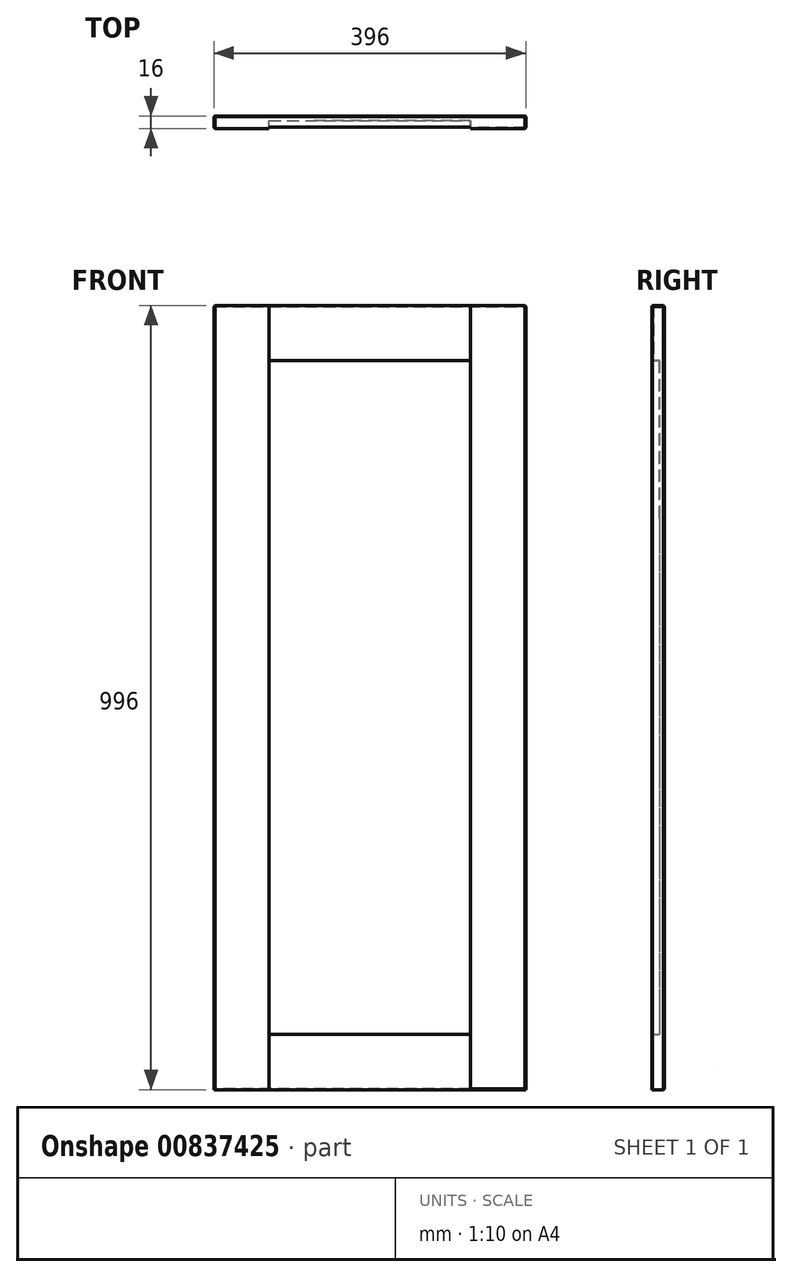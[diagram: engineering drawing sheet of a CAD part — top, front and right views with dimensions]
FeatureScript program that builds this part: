
annotation { "Feature Type Name" : "Feature", "Feature Type Description" : "" }
export const myFeature = defineFeature(function(context is Context, id is Id, definition is map)
    precondition{}
    {
        {
            var Q0;
            Q0=qCreatedBy(makeId("Front.planeOp"),FACE);
            var sketch = newSketch(context, id + "F0", { "sketchPlane" : qUnion([Q0])});
            skLineSegment(sketch, "E0.bottom", {"start": v(0, 0) * mm, "end": v(35.9, 0) * mm});
            skLineSegment(sketch, "E0.top", {"start": v(0, 30.12) * mm, "end": v(35.9, 30.12) * mm});
            skLineSegment(sketch, "E0.left", {"start": v(0, 0) * mm, "end": v(0, 30.12) * mm});
            skLineSegment(sketch, "E0.right", {"start": v(35.9, 0) * mm, "end": v(35.9, 30.12) * mm});
            skSolve(sketch);
        }
        {
            var Q0;
            Q0=makeQuery(id+"F0.imprint","IMPRINT",FACE,{"disambiguationData":[TD([[makeQuery(id+"F0.imprint","IMPRINT",EDGE,{"derivedFrom":sQuery(id+"F0.wireOp",EDGE,"E0.bottom")}),1.0]])]});
            extrude(context, id + "F1", {"entities" : qUnion([Q0]), "depth" : 16 * mm, "offsetDistance" : 25.4 * mm});
        }
        {
            var Q0;
            Q0=makeQuery(id+"F1.opExtrude","SWEPT_FACE",FACE,{"disambiguationData":[OSD([sQuery(id+"F0.wireOp",EDGE,"E0.left")])]});
            extrude(context, id + "F2", {"entities" : qUnion([Q0]), "operationType" : NewBodyOperationType.ADD, "oppositeDirection" : true, "depth" : 196 * mm, "offsetDistance" : 25 * mm});
        }
        {
            var Q0;
            {var subQ0=sQuery(id+"F0.wireOp",EDGE,"E0.bottom");Q0=makeQuery(id+"F2.boolean.opBoolean","MERGE",FACE,{"derivedFrom":[makeQuery(id+"F1.opExtrude","SWEPT_FACE",FACE,{"disambiguationData":[OSD([subQ0])]}),makeQuery(id+"F2.opExtrude","SWEPT_FACE",FACE,{"disambiguationData":[OSD([subQ0,sQuery(id+"F0.wireOp",EDGE,"E0.left")])]})]});}
            extrude(context, id + "F3", {"entities" : qUnion([Q0]), "operationType" : NewBodyOperationType.ADD, "oppositeDirection" : true, "depth" : 796 * mm, "offsetDistance" : 25 * mm});
        }
        {
            var Q0;
            {var subQ0=sQuery(id+"F0.wireOp",EDGE,"E0.left");var subQ1=sQuery(id+"F0.wireOp",EDGE,"E0.bottom");Q0=makeQuery(id+"F3.boolean.opBoolean","MERGE",FACE,{"derivedFrom":[makeQuery(id+"F2.boolean.opBoolean","MERGE",FACE,{"derivedFrom":[makeQuery(id+"F1.opExtrude","CAP_FACE",FACE,{"disambiguationData":[OSD([subQ1,sQuery(id+"F0.wireOp",EDGE,"E0.top"),subQ0,sQuery(id+"F0.wireOp",EDGE,"E0.right")])],"isStart":false}),makeQuery(id+"F2.opExtrude","SWEPT_FACE",FACE,{"disambiguationData":[OSD([subQ0]),TDD([makeQuery(id+"F1.opExtrude","CAP_EDGE",EDGE,{"disambiguationData":[OSD([subQ0])],"isStart":false})])]})]}),makeQuery(id+"F3.opExtrude","SWEPT_FACE",FACE,{"disambiguationData":[OSD([subQ1,subQ0]),TDD([makeQuery(id+"F2.boolean.opBoolean","MERGE",EDGE,{"derivedFrom":[makeQuery(id+"F1.opExtrude","CAP_EDGE",EDGE,{"disambiguationData":[OSD([subQ1])],"isStart":false}),makeQuery(id+"F2.opExtrude","SWEPT_EDGE",EDGE,{"disambiguationData":[OSD([subQ1,subQ0]),TDD([makeQuery(id+"F1.opExtrude","CAP_VERTEX",VERTEX,{"disambiguationData":[OSD([subQ1,subQ0])],"isStart":false})])]})]})])]})]});}
            var sketch = newSketch(context, id + "F4", { "sketchPlane" : qUnion([Q0])});
            skLineSegment(sketch, "E1.bottom", {"start": v(0, 796) * mm, "end": v(42.19, 796) * mm});
            skLineSegment(sketch, "E1.top", {"start": v(0, 751.57) * mm, "end": v(42.19, 751.57) * mm});
            skLineSegment(sketch, "E1.left", {"start": v(0, 796) * mm, "end": v(0, 751.57) * mm});
            skLineSegment(sketch, "E1.right", {"start": v(42.19, 796) * mm, "end": v(42.19, 751.57) * mm});
            skLineSegment(sketch, "E2.bottom", {"start": v(196, 796) * mm, "end": v(153.6, 796) * mm});
            skLineSegment(sketch, "E2.top", {"start": v(196, 746.75) * mm, "end": v(153.6, 746.75) * mm});
            skLineSegment(sketch, "E2.left", {"start": v(196, 796) * mm, "end": v(196, 746.75) * mm});
            skLineSegment(sketch, "E2.right", {"start": v(153.6, 796) * mm, "end": v(153.6, 746.75) * mm});
            skSolve(sketch);
        }
        {
            var Q0;
            Q0=makeQuery(id+"F4.imprint","IMPRINT",FACE,{"disambiguationData":[TD([[makeQuery(id+"F4.imprint","IMPRINT",EDGE,{"derivedFrom":sQuery(id+"F4.wireOp",EDGE,"E1.bottom")}),-1.0]])]});
            var Q1;
            Q1=makeQuery(id+"F4.imprint","IMPRINT",FACE,{"disambiguationData":[TD([[makeQuery(id+"F4.imprint","IMPRINT",EDGE,{"derivedFrom":sQuery(id+"F4.wireOp",EDGE,"E2.bottom")}),-1.0]])]});
            extrude(context, id + "F5", {"entities" : qUnion([Q0, Q1]), "operationType" : NewBodyOperationType.ADD, "depth" : 25 * mm, "offsetDistance" : 25 * mm});
        }
        {
            var Q0;
            {var subQ0=sQuery(id+"F0.wireOp",EDGE,"E0.left");var subQ1=sQuery(id+"F0.wireOp",EDGE,"E0.bottom");Q0=makeQuery(id+"F3.boolean.opBoolean","MERGE",FACE,{"derivedFrom":[makeQuery(id+"F2.boolean.opBoolean","MERGE",FACE,{"derivedFrom":[makeQuery(id+"F1.opExtrude","CAP_FACE",FACE,{"disambiguationData":[OSD([subQ1,sQuery(id+"F0.wireOp",EDGE,"E0.top"),subQ0,sQuery(id+"F0.wireOp",EDGE,"E0.right")])],"isStart":false}),makeQuery(id+"F2.opExtrude","SWEPT_FACE",FACE,{"disambiguationData":[OSD([subQ0]),TDD([makeQuery(id+"F1.opExtrude","CAP_EDGE",EDGE,{"disambiguationData":[OSD([subQ0])],"isStart":false})])]})]}),makeQuery(id+"F3.opExtrude","SWEPT_FACE",FACE,{"disambiguationData":[OSD([subQ1,subQ0]),TDD([makeQuery(id+"F2.boolean.opBoolean","MERGE",EDGE,{"derivedFrom":[makeQuery(id+"F1.opExtrude","CAP_EDGE",EDGE,{"disambiguationData":[OSD([subQ1])],"isStart":false}),makeQuery(id+"F2.opExtrude","SWEPT_EDGE",EDGE,{"disambiguationData":[OSD([subQ1,subQ0]),TDD([makeQuery(id+"F1.opExtrude","CAP_VERTEX",VERTEX,{"disambiguationData":[OSD([subQ1,subQ0])],"isStart":false})])]})]})])]})]});}
            var sketch = newSketch(context, id + "F6", { "sketchPlane" : qUnion([Q0])});
            skLineSegment(sketch, "E3.bottom", {"start": v(196, 0) * mm, "end": v(163.38, 0) * mm});
            skLineSegment(sketch, "E3.top", {"start": v(196, 46.55) * mm, "end": v(163.38, 46.55) * mm});
            skLineSegment(sketch, "E3.left", {"start": v(196, 0) * mm, "end": v(196, 46.55) * mm});
            skLineSegment(sketch, "E3.right", {"start": v(163.38, 0) * mm, "end": v(163.38, 46.55) * mm});
            skLineSegment(sketch, "E4.bottom", {"start": v(0, 0) * mm, "end": v(50.28, 0) * mm});
            skLineSegment(sketch, "E4.top", {"start": v(0, 44.4) * mm, "end": v(50.28, 44.4) * mm});
            skLineSegment(sketch, "E4.left", {"start": v(0, 0) * mm, "end": v(0, 44.4) * mm});
            skLineSegment(sketch, "E4.right", {"start": v(50.28, 0) * mm, "end": v(50.28, 44.4) * mm});
            skSolve(sketch);
        }
        {
            var Q0;
            Q0=makeQuery(id+"F6.imprint","IMPRINT",FACE,{"disambiguationData":[TD([[makeQuery(id+"F6.imprint","IMPRINT",EDGE,{"derivedFrom":sQuery(id+"F6.wireOp",EDGE,"E3.bottom")}),1.0]])]});
            var Q1;
            Q1=makeQuery(id+"F6.imprint","IMPRINT",FACE,{"disambiguationData":[TD([[makeQuery(id+"F6.imprint","IMPRINT",EDGE,{"derivedFrom":sQuery(id+"F6.wireOp",EDGE,"E4.bottom")}),1.0]])]});
            extrude(context, id + "F7", {"entities" : qUnion([Q0, Q1]), "operationType" : NewBodyOperationType.ADD, "depth" : 25 * mm, "offsetDistance" : 25 * mm});
        }
        {
            var Q0;
            Q0=makeQuery(id+"F7.opExtrude","SWEPT_FACE",FACE,{"disambiguationData":[OSD([sQuery(id+"F6.wireOp",EDGE,"E4.right")])]});
            extrude(context, id + "F8", {"entities" : qUnion([Q0]), "operationType" : NewBodyOperationType.ADD, "depth" : 19.72 * mm, "offsetDistance" : 25 * mm});
        }
        {
            var Q0;
            {var subQ0=sQuery(id+"F6.wireOp",EDGE,"E4.top");Q0=makeQuery(id+"F8.boolean.opBoolean","MERGE",FACE,{"derivedFrom":[makeQuery(id+"F7.opExtrude","SWEPT_FACE",FACE,{"disambiguationData":[OSD([subQ0])]}),makeQuery(id+"F8.opExtrude","SWEPT_FACE",FACE,{"disambiguationData":[OSD([subQ0,sQuery(id+"F6.wireOp",EDGE,"E4.right")])]})]});}
            extrude(context, id + "F9", {"entities" : qUnion([Q0]), "operationType" : NewBodyOperationType.ADD, "depth" : 25.6 * mm, "offsetDistance" : 25 * mm});
        }
        {
            var Q0;
            Q0=makeQuery(id+"F7.opExtrude","SWEPT_FACE",FACE,{"disambiguationData":[OSD([sQuery(id+"F6.wireOp",EDGE,"E3.right")])]});
            extrude(context, id + "F10", {"entities" : qUnion([Q0]), "operationType" : NewBodyOperationType.ADD, "depth" : 37.38 * mm, "offsetDistance" : 25 * mm});
        }
        {
            var Q0;
            {var subQ0=sQuery(id+"F6.wireOp",EDGE,"E3.top");Q0=makeQuery(id+"F10.boolean.opBoolean","MERGE",FACE,{"derivedFrom":[makeQuery(id+"F7.opExtrude","SWEPT_FACE",FACE,{"disambiguationData":[OSD([subQ0])]}),makeQuery(id+"F10.opExtrude","SWEPT_FACE",FACE,{"disambiguationData":[OSD([subQ0,sQuery(id+"F6.wireOp",EDGE,"E3.right")])]})]});}
            extrude(context, id + "F11", {"entities" : qUnion([Q0]), "operationType" : NewBodyOperationType.ADD, "depth" : 23.45 * mm, "offsetDistance" : 25 * mm});
        }
        {
            var Q0;
            Q0=makeQuery(id+"F5.opExtrude","SWEPT_FACE",FACE,{"disambiguationData":[OSD([sQuery(id+"F4.wireOp",EDGE,"E1.right")])]});
            extrude(context, id + "F12", {"entities" : qUnion([Q0]), "operationType" : NewBodyOperationType.ADD, "depth" : 27.8 * mm, "offsetDistance" : 25 * mm});
        }
        {
            var Q0;
            {var subQ0=sQuery(id+"F4.wireOp",EDGE,"E1.top");Q0=makeQuery(id+"F12.boolean.opBoolean","MERGE",FACE,{"derivedFrom":[makeQuery(id+"F5.opExtrude","SWEPT_FACE",FACE,{"disambiguationData":[OSD([subQ0])]}),makeQuery(id+"F12.opExtrude","SWEPT_FACE",FACE,{"disambiguationData":[OSD([subQ0,sQuery(id+"F4.wireOp",EDGE,"E1.right")])]})]});}
            extrude(context, id + "F13", {"entities" : qUnion([Q0]), "operationType" : NewBodyOperationType.ADD, "depth" : 25.57 * mm, "offsetDistance" : 25 * mm});
        }
        {
            var Q0;
            Q0=makeQuery(id+"F5.opExtrude","SWEPT_FACE",FACE,{"disambiguationData":[OSD([sQuery(id+"F4.wireOp",EDGE,"E2.top")])]});
            extrude(context, id + "F14", {"entities" : qUnion([Q0]), "operationType" : NewBodyOperationType.ADD, "depth" : 20.75 * mm, "offsetDistance" : 25 * mm});
        }
        {
            var Q0;
            {var subQ0=sQuery(id+"F4.wireOp",EDGE,"E2.right");Q0=makeQuery(id+"F14.boolean.opBoolean","MERGE",FACE,{"derivedFrom":[makeQuery(id+"F5.opExtrude","SWEPT_FACE",FACE,{"disambiguationData":[OSD([subQ0])]}),makeQuery(id+"F14.opExtrude","SWEPT_FACE",FACE,{"disambiguationData":[OSD([sQuery(id+"F4.wireOp",EDGE,"E2.top"),subQ0])]})]});}
            extrude(context, id + "F15", {"entities" : qUnion([Q0]), "operationType" : NewBodyOperationType.ADD, "depth" : 27.6 * mm, "offsetDistance" : 25 * mm});
        }
        {
            var Q0;
            {var subQ0=sQuery(id+"F0.wireOp",EDGE,"E0.left");var subQ1=sQuery(id+"F0.wireOp",EDGE,"E0.bottom");Q0=makeQuery(id+"F3.boolean.opBoolean","MERGE",FACE,{"derivedFrom":[makeQuery(id+"F2.boolean.opBoolean","MERGE",FACE,{"derivedFrom":[makeQuery(id+"F1.opExtrude","CAP_FACE",FACE,{"disambiguationData":[OSD([subQ1,sQuery(id+"F0.wireOp",EDGE,"E0.top"),subQ0,sQuery(id+"F0.wireOp",EDGE,"E0.right")])],"isStart":false}),makeQuery(id+"F2.opExtrude","SWEPT_FACE",FACE,{"disambiguationData":[OSD([subQ0]),TDD([makeQuery(id+"F1.opExtrude","CAP_EDGE",EDGE,{"disambiguationData":[OSD([subQ0])],"isStart":false})])]})]}),makeQuery(id+"F3.opExtrude","SWEPT_FACE",FACE,{"disambiguationData":[OSD([subQ1,subQ0]),TDD([makeQuery(id+"F2.boolean.opBoolean","MERGE",EDGE,{"derivedFrom":[makeQuery(id+"F1.opExtrude","CAP_EDGE",EDGE,{"disambiguationData":[OSD([subQ1])],"isStart":false}),makeQuery(id+"F2.opExtrude","SWEPT_EDGE",EDGE,{"disambiguationData":[OSD([subQ1,subQ0]),TDD([makeQuery(id+"F1.opExtrude","CAP_VERTEX",VERTEX,{"disambiguationData":[OSD([subQ1,subQ0])],"isStart":false})])]})]})])]})]});}
            var sketch = newSketch(context, id + "F16", { "sketchPlane" : qUnion([Q0])});
            skLineSegment(sketch, "E5.bottom", {"start": v(70, 726) * mm, "end": v(126, 726) * mm});
            skLineSegment(sketch, "E5.top", {"start": v(70, 70) * mm, "end": v(126, 70) * mm});
            skLineSegment(sketch, "E5.left", {"start": v(70, 726) * mm, "end": v(70, 70) * mm});
            skLineSegment(sketch, "E5.right", {"start": v(126, 726) * mm, "end": v(126, 70) * mm});
            skSolve(sketch);
        }
        {
            var Q0;
            Q0=makeQuery(id+"F16.imprint","IMPRINT",FACE,{"disambiguationData":[TD([[makeQuery(id+"F16.imprint","IMPRINT",EDGE,{"derivedFrom":sQuery(id+"F16.wireOp",EDGE,"E5.top")}),1.0]])]});
            extrude(context, id + "F17", {"entities" : qUnion([Q0]), "operationType" : NewBodyOperationType.REMOVE, "oppositeDirection" : true, "depth" : 10 * mm, "offsetDistance" : 25 * mm});
        }
        {
            var Q0;
            {var subQ2=sQuery(id+"F0.wireOp",EDGE,"E0.left");var subQ3=sQuery(id+"F0.wireOp",EDGE,"E0.bottom");var subQ4=makeQuery(id+"F1.opExtrude","CAP_FACE",FACE,{"disambiguationData":[OSD([subQ3,sQuery(id+"F0.wireOp",EDGE,"E0.top"),subQ2,sQuery(id+"F0.wireOp",EDGE,"E0.right")])],"isStart":false});var subQ7=makeQuery(id+"F3.opExtrude","SWEPT_FACE",FACE,{"disambiguationData":[OSD([subQ3,subQ2]),TDD([makeQuery(id+"F2.boolean.opBoolean","MERGE",EDGE,{"derivedFrom":[makeQuery(id+"F1.opExtrude","CAP_EDGE",EDGE,{"disambiguationData":[OSD([subQ3])],"isStart":false}),makeQuery(id+"F2.opExtrude","SWEPT_EDGE",EDGE,{"disambiguationData":[OSD([subQ3,subQ2]),TDD([makeQuery(id+"F1.opExtrude","CAP_VERTEX",VERTEX,{"disambiguationData":[OSD([subQ3,subQ2])],"isStart":false})])]})]})])]});var subQ8=makeQuery(id+"F2.opExtrude","SWEPT_FACE",FACE,{"disambiguationData":[OSD([subQ2]),TDD([makeQuery(id+"F1.opExtrude","CAP_EDGE",EDGE,{"disambiguationData":[OSD([subQ2])],"isStart":false})])]});Q0=makeQuery(id+"F17.boolean.opBoolean","SPLIT",FACE,{"disambiguationData":[TD([makeQuery(id+"F1.opExtrude","SWEPT_FACE",FACE,{"disambiguationData":[OSD([subQ3])]})])],"derivedFrom":makeQuery(id+"F3.boolean.opBoolean","MERGE",FACE,{"derivedFrom":[makeQuery(id+"F2.boolean.opBoolean","MERGE",FACE,{"derivedFrom":[subQ4,subQ8]}),subQ7]})});}
            var Q1;
            {var subQ2=sQuery(id+"F4.wireOp",EDGE,"E1.bottom");var subQ3=sQuery(id+"F0.wireOp",EDGE,"E0.left");var subQ4=sQuery(id+"F0.wireOp",EDGE,"E0.bottom");var subQ6=makeQuery(id+"F1.opExtrude","CAP_FACE",FACE,{"disambiguationData":[OSD([subQ4,sQuery(id+"F0.wireOp",EDGE,"E0.top"),subQ3,sQuery(id+"F0.wireOp",EDGE,"E0.right")])],"isStart":false});var subQ7=makeQuery(id+"F2.opExtrude","SWEPT_FACE",FACE,{"disambiguationData":[OSD([subQ3]),TDD([makeQuery(id+"F1.opExtrude","CAP_EDGE",EDGE,{"disambiguationData":[OSD([subQ3])],"isStart":false})])]});var subQ8=makeQuery(id+"F3.opExtrude","SWEPT_FACE",FACE,{"disambiguationData":[OSD([subQ4,subQ3]),TDD([makeQuery(id+"F2.boolean.opBoolean","MERGE",EDGE,{"derivedFrom":[makeQuery(id+"F1.opExtrude","CAP_EDGE",EDGE,{"disambiguationData":[OSD([subQ4])],"isStart":false}),makeQuery(id+"F2.opExtrude","SWEPT_EDGE",EDGE,{"disambiguationData":[OSD([subQ4,subQ3]),TDD([makeQuery(id+"F1.opExtrude","CAP_VERTEX",VERTEX,{"disambiguationData":[OSD([subQ4,subQ3])],"isStart":false})])]})]})])]});Q1=makeQuery(id+"F17.boolean.opBoolean","SPLIT",FACE,{"disambiguationData":[TD([makeQuery(id+"F5.opExtrude","SWEPT_FACE",FACE,{"disambiguationData":[OSD([subQ2])]})])],"derivedFrom":makeQuery(id+"F3.boolean.opBoolean","MERGE",FACE,{"derivedFrom":[makeQuery(id+"F2.boolean.opBoolean","MERGE",FACE,{"derivedFrom":[subQ6,subQ7]}),subQ8]})});}
            extrude(context, id + "F18", {"entities" : qUnion([Q0, Q1]), "operationType" : NewBodyOperationType.REMOVE, "oppositeDirection" : true, "depth" : 2 * mm, "offsetDistance" : 25 * mm});
        }
        {
            var Q0;
            {var subQ0=sQuery(id+"F4.wireOp",EDGE,"E1.right");var subQ1=sQuery(id+"F4.wireOp",EDGE,"E1.top");Q0=makeQuery(id+"F13.boolean.opBoolean","MERGE",FACE,{"derivedFrom":[makeQuery(id+"F12.boolean.opBoolean","MERGE",FACE,{"derivedFrom":[makeQuery(id+"F5.opExtrude","CAP_FACE",FACE,{"disambiguationData":[OSD([sQuery(id+"F4.wireOp",EDGE,"E1.bottom"),subQ1,sQuery(id+"F4.wireOp",EDGE,"E1.left"),subQ0])],"isStart":false}),makeQuery(id+"F12.opExtrude","SWEPT_FACE",FACE,{"disambiguationData":[OSD([subQ0]),TDD([makeQuery(id+"F5.opExtrude","CAP_EDGE",EDGE,{"disambiguationData":[OSD([subQ0])],"isStart":false})])]})]}),makeQuery(id+"F13.opExtrude","SWEPT_FACE",FACE,{"disambiguationData":[OSD([subQ1,subQ0]),TDD([makeQuery(id+"F12.boolean.opBoolean","MERGE",EDGE,{"derivedFrom":[makeQuery(id+"F5.opExtrude","CAP_EDGE",EDGE,{"disambiguationData":[OSD([subQ1])],"isStart":false}),makeQuery(id+"F12.opExtrude","SWEPT_EDGE",EDGE,{"disambiguationData":[OSD([subQ1,subQ0]),TDD([makeQuery(id+"F5.opExtrude","CAP_VERTEX",VERTEX,{"disambiguationData":[OSD([subQ1,subQ0])],"isStart":false})])]})]})])]})]});}
            var Q1;
            {var subQ0=sQuery(id+"F4.wireOp",EDGE,"E2.right");var subQ1=sQuery(id+"F4.wireOp",EDGE,"E2.top");Q1=makeQuery(id+"F15.boolean.opBoolean","MERGE",FACE,{"derivedFrom":[makeQuery(id+"F14.boolean.opBoolean","MERGE",FACE,{"derivedFrom":[makeQuery(id+"F5.opExtrude","CAP_FACE",FACE,{"disambiguationData":[OSD([sQuery(id+"F4.wireOp",EDGE,"E2.bottom"),subQ1,sQuery(id+"F4.wireOp",EDGE,"E2.left"),subQ0])],"isStart":false}),makeQuery(id+"F14.opExtrude","SWEPT_FACE",FACE,{"disambiguationData":[OSD([subQ1]),TDD([makeQuery(id+"F5.opExtrude","CAP_EDGE",EDGE,{"disambiguationData":[OSD([subQ1])],"isStart":false})])]})]}),makeQuery(id+"F15.opExtrude","SWEPT_FACE",FACE,{"disambiguationData":[OSD([subQ1,subQ0]),TDD([makeQuery(id+"F14.boolean.opBoolean","MERGE",EDGE,{"derivedFrom":[makeQuery(id+"F5.opExtrude","CAP_EDGE",EDGE,{"disambiguationData":[OSD([subQ0])],"isStart":false}),makeQuery(id+"F14.opExtrude","SWEPT_EDGE",EDGE,{"disambiguationData":[OSD([subQ1,subQ0]),TDD([makeQuery(id+"F5.opExtrude","CAP_VERTEX",VERTEX,{"disambiguationData":[OSD([subQ1,subQ0])],"isStart":false})])]})]})])]})]});}
            var Q2;
            {var subQ0=sQuery(id+"F6.wireOp",EDGE,"E4.right");var subQ1=sQuery(id+"F6.wireOp",EDGE,"E4.top");Q2=makeQuery(id+"F9.boolean.opBoolean","MERGE",FACE,{"derivedFrom":[makeQuery(id+"F8.boolean.opBoolean","MERGE",FACE,{"derivedFrom":[makeQuery(id+"F7.opExtrude","CAP_FACE",FACE,{"disambiguationData":[OSD([sQuery(id+"F6.wireOp",EDGE,"E4.bottom"),subQ1,sQuery(id+"F6.wireOp",EDGE,"E4.left"),subQ0])],"isStart":false}),makeQuery(id+"F8.opExtrude","SWEPT_FACE",FACE,{"disambiguationData":[OSD([subQ0]),TDD([makeQuery(id+"F7.opExtrude","CAP_EDGE",EDGE,{"disambiguationData":[OSD([subQ0])],"isStart":false})])]})]}),makeQuery(id+"F9.opExtrude","SWEPT_FACE",FACE,{"disambiguationData":[OSD([subQ1,subQ0]),TDD([makeQuery(id+"F8.boolean.opBoolean","MERGE",EDGE,{"derivedFrom":[makeQuery(id+"F7.opExtrude","CAP_EDGE",EDGE,{"disambiguationData":[OSD([subQ1])],"isStart":false}),makeQuery(id+"F8.opExtrude","SWEPT_EDGE",EDGE,{"disambiguationData":[OSD([subQ1,subQ0]),TDD([makeQuery(id+"F7.opExtrude","CAP_VERTEX",VERTEX,{"disambiguationData":[OSD([subQ1,subQ0])],"isStart":false})])]})]})])]})]});}
            var Q3;
            {var subQ0=sQuery(id+"F6.wireOp",EDGE,"E3.right");var subQ1=sQuery(id+"F6.wireOp",EDGE,"E3.top");Q3=makeQuery(id+"F11.boolean.opBoolean","MERGE",FACE,{"derivedFrom":[makeQuery(id+"F10.boolean.opBoolean","MERGE",FACE,{"derivedFrom":[makeQuery(id+"F7.opExtrude","CAP_FACE",FACE,{"disambiguationData":[OSD([sQuery(id+"F6.wireOp",EDGE,"E3.bottom"),subQ1,sQuery(id+"F6.wireOp",EDGE,"E3.left"),subQ0])],"isStart":false}),makeQuery(id+"F10.opExtrude","SWEPT_FACE",FACE,{"disambiguationData":[OSD([subQ0]),TDD([makeQuery(id+"F7.opExtrude","CAP_EDGE",EDGE,{"disambiguationData":[OSD([subQ0])],"isStart":false})])]})]}),makeQuery(id+"F11.opExtrude","SWEPT_FACE",FACE,{"disambiguationData":[OSD([subQ1,subQ0]),TDD([makeQuery(id+"F10.boolean.opBoolean","MERGE",EDGE,{"derivedFrom":[makeQuery(id+"F7.opExtrude","CAP_EDGE",EDGE,{"disambiguationData":[OSD([subQ1])],"isStart":false}),makeQuery(id+"F10.opExtrude","SWEPT_EDGE",EDGE,{"disambiguationData":[OSD([subQ1,subQ0]),TDD([makeQuery(id+"F7.opExtrude","CAP_VERTEX",VERTEX,{"disambiguationData":[OSD([subQ1,subQ0])],"isStart":false})])]})]})])]})]});}
            extrude(context, id + "F19", {"entities" : qUnion([Q0, Q1, Q2, Q3]), "operationType" : NewBodyOperationType.REMOVE, "oppositeDirection" : true, "depth" : 25 * mm, "offsetDistance" : 25 * mm});
        }
        {
            var Q0;
            {var subQ0=sQuery(id+"F4.wireOp",EDGE,"E2.left");var subQ1=sQuery(id+"F0.wireOp",EDGE,"E0.left");var subQ2=sQuery(id+"F0.wireOp",EDGE,"E0.bottom");var subQ3=sQuery(id+"F6.wireOp",EDGE,"E3.left");Q0=makeQuery(id+"F14.boolean.opBoolean","MERGE",FACE,{"derivedFrom":[makeQuery(id+"F11.boolean.opBoolean","MERGE",FACE,{"derivedFrom":[makeQuery(id+"F7.boolean.opBoolean","MERGE",FACE,{"derivedFrom":[makeQuery(id+"F5.boolean.opBoolean","MERGE",FACE,{"derivedFrom":[makeQuery(id+"F3.boolean.opBoolean","MERGE",FACE,{"derivedFrom":[makeQuery(id+"F2.opExtrude","CAP_FACE",FACE,{"disambiguationData":[OSD([subQ1])],"isStart":false}),makeQuery(id+"F3.opExtrude","SWEPT_FACE",FACE,{"disambiguationData":[OSD([subQ2,subQ1]),TDD([makeQuery(id+"F2.opExtrude","CAP_EDGE",EDGE,{"disambiguationData":[OSD([subQ2,subQ1])],"isStart":false})])]})]}),makeQuery(id+"F5.opExtrude","SWEPT_FACE",FACE,{"disambiguationData":[OSD([subQ0])]})]}),makeQuery(id+"F7.opExtrude","SWEPT_FACE",FACE,{"disambiguationData":[OSD([subQ3])]})]}),makeQuery(id+"F11.opExtrude","SWEPT_FACE",FACE,{"disambiguationData":[OSD([subQ2,subQ1,sQuery(id+"F6.wireOp",EDGE,"E3.top"),subQ3])]})]}),makeQuery(id+"F14.opExtrude","SWEPT_FACE",FACE,{"disambiguationData":[OSD([subQ2,subQ1,sQuery(id+"F4.wireOp",EDGE,"E2.top"),subQ0])]})]});}
            extrude(context, id + "F20", {"entities" : qUnion([Q0]), "operationType" : NewBodyOperationType.ADD, "depth" : 200 * mm, "offsetDistance" : 25 * mm});
        }
        {
            var Q0;
            {var subQ0=sQuery(id+"F4.wireOp",EDGE,"E2.right");var subQ1=sQuery(id+"F4.wireOp",EDGE,"E2.top");Q0=makeQuery(id+"F18.boolean.opBoolean","MERGE",FACE,{"derivedFrom":[makeQuery(id+"F15.opExtrude","CAP_FACE",FACE,{"disambiguationData":[OSD([subQ1,subQ0])],"isStart":false}),makeQuery(id+"F18.opExtrude","SWEPT_FACE",FACE,{"disambiguationData":[OSD([subQ1,subQ0])]})]});}
            var Q1;
            {var subQ0=sQuery(id+"F6.wireOp",EDGE,"E3.right");var subQ1=sQuery(id+"F6.wireOp",EDGE,"E3.top");Q1=makeQuery(id+"F18.boolean.opBoolean","MERGE",FACE,{"derivedFrom":[makeQuery(id+"F11.boolean.opBoolean","MERGE",FACE,{"derivedFrom":[makeQuery(id+"F10.opExtrude","CAP_FACE",FACE,{"disambiguationData":[OSD([subQ0])],"isStart":false}),makeQuery(id+"F11.opExtrude","SWEPT_FACE",FACE,{"disambiguationData":[OSD([subQ1,subQ0]),TDD([makeQuery(id+"F10.opExtrude","CAP_EDGE",EDGE,{"disambiguationData":[OSD([subQ1,subQ0])],"isStart":false})])]})]}),makeQuery(id+"F17.boolean.opBoolean","COPY",FACE,{"derivedFrom":makeQuery(id+"F17.opExtrude","SWEPT_FACE",FACE,{"disambiguationData":[OSD([sQuery(id+"F16.wireOp",EDGE,"E5.right")])]})}),makeQuery(id+"F18.opExtrude","SWEPT_FACE",FACE,{"disambiguationData":[OSD([subQ1,subQ0])]})]});}
            extrude(context, id + "F21", {"entities" : qUnion([Q0, Q1]), "operationType" : NewBodyOperationType.REMOVE, "oppositeDirection" : true, "depth" : 200 * mm, "offsetDistance" : 25 * mm});
        }
        {
            var Q0;
            {var subQ0=sQuery(id+"F4.wireOp",EDGE,"E2.bottom");var subQ1=sQuery(id+"F0.wireOp",EDGE,"E0.left");var subQ2=sQuery(id+"F0.wireOp",EDGE,"E0.bottom");var subQ3=sQuery(id+"F4.wireOp",EDGE,"E1.bottom");Q0=makeQuery(id+"F20.boolean.opBoolean","MERGE",FACE,{"derivedFrom":[makeQuery(id+"F15.boolean.opBoolean","MERGE",FACE,{"derivedFrom":[makeQuery(id+"F12.boolean.opBoolean","MERGE",FACE,{"derivedFrom":[makeQuery(id+"F5.boolean.opBoolean","MERGE",FACE,{"derivedFrom":[makeQuery(id+"F3.opExtrude","CAP_FACE",FACE,{"disambiguationData":[OSD([subQ2,subQ1])],"isStart":false}),makeQuery(id+"F5.opExtrude","SWEPT_FACE",FACE,{"disambiguationData":[OSD([subQ3])]}),makeQuery(id+"F5.opExtrude","SWEPT_FACE",FACE,{"disambiguationData":[OSD([subQ0])]})]}),makeQuery(id+"F12.opExtrude","SWEPT_FACE",FACE,{"disambiguationData":[OSD([subQ2,subQ1,subQ3,sQuery(id+"F4.wireOp",EDGE,"E1.right")])]})]}),makeQuery(id+"F15.opExtrude","SWEPT_FACE",FACE,{"disambiguationData":[OSD([subQ2,subQ1,subQ0,sQuery(id+"F4.wireOp",EDGE,"E2.right")])]})]}),makeQuery(id+"F20.opExtrude","SWEPT_FACE",FACE,{"disambiguationData":[OSD([subQ2,subQ1,subQ0,sQuery(id+"F4.wireOp",EDGE,"E2.left")])]})]});}
            extrude(context, id + "F22", {"entities" : qUnion([Q0]), "operationType" : NewBodyOperationType.ADD, "depth" : 200 * mm, "offsetDistance" : 25 * mm});
        }
        {
            var Q0;
            Q0=makeQuery(id+"F17.boolean.opBoolean","COPY",FACE,{"derivedFrom":makeQuery(id+"F17.opExtrude","SWEPT_FACE",FACE,{"disambiguationData":[OSD([sQuery(id+"F16.wireOp",EDGE,"E5.bottom")])]})});
            var Q1;
            {var subQ0=sQuery(id+"F16.wireOp",EDGE,"E5.right");var subQ1=sQuery(id+"F16.wireOp",EDGE,"E5.bottom");var subQ2=sQuery(id+"F4.wireOp",EDGE,"E2.right");var subQ3=sQuery(id+"F4.wireOp",EDGE,"E2.top");var subQ4=makeQuery(id+"F17.boolean.opBoolean","COPY",EDGE,{"derivedFrom":makeQuery(id+"F17.opExtrude","SWEPT_EDGE",EDGE,{"disambiguationData":[OSD([subQ3,subQ2,subQ1,subQ0])]})});Q1=makeQuery(id+"F21.boolean.opBoolean","COPY",FACE,{"derivedFrom":makeQuery(id+"F21.opExtrude","SWEPT_FACE",FACE,{"disambiguationData":[OSD([subQ3,subQ2,subQ1,subQ0]),TDD([makeQuery(id+"F18.boolean.opBoolean","MERGE",EDGE,{"derivedFrom":[subQ4,makeQuery(id+"F18.opExtrude","SWEPT_EDGE",EDGE,{"disambiguationData":[OSD([subQ3,subQ2,subQ1,subQ0])]})]}),makeQuery(id+"F18.boolean.opBoolean","SPLIT",EDGE,{"derivedFrom":subQ4})])]})});}
            extrude(context, id + "F23", {"entities" : qUnion([Q0, Q1]), "operationType" : NewBodyOperationType.REMOVE, "oppositeDirection" : true, "depth" : 200 * mm, "offsetDistance" : 25 * mm});
        }
        {
            var Q0;
            {var subQ0=sQuery(id+"F6.wireOp",EDGE,"E3.bottom");Q0=makeQuery(id+"F20.boolean.opBoolean","MERGE",EDGE,{"derivedFrom":[makeQuery(id+"F19.boolean.opBoolean","COPY",EDGE,{"derivedFrom":makeQuery(id+"F19.opExtrude","CAP_EDGE",EDGE,{"disambiguationData":[OSD([sQuery(id+"F0.wireOp",EDGE,"E0.bottom"),sQuery(id+"F0.wireOp",EDGE,"E0.left"),subQ0,sQuery(id+"F6.wireOp",EDGE,"E3.right")])],"isStart":false})}),makeQuery(id+"F20.opExtrude","SWEPT_EDGE",EDGE,{"disambiguationData":[OSD([subQ0,sQuery(id+"F6.wireOp",EDGE,"E3.left")])]})]});}
            var Q1;
            {var subQ0=sQuery(id+"F4.wireOp",EDGE,"E2.left");Q1=makeQuery(id+"F22.boolean.opBoolean","MERGE",EDGE,{"derivedFrom":[makeQuery(id+"F20.opExtrude","CAP_EDGE",EDGE,{"disambiguationData":[OSD([sQuery(id+"F0.wireOp",EDGE,"E0.bottom"),sQuery(id+"F0.wireOp",EDGE,"E0.left"),sQuery(id+"F4.wireOp",EDGE,"E2.top"),subQ0,sQuery(id+"F6.wireOp",EDGE,"E3.top"),sQuery(id+"F6.wireOp",EDGE,"E3.left")])],"isStart":false}),makeQuery(id+"F22.opExtrude","SWEPT_EDGE",EDGE,{"disambiguationData":[OSD([sQuery(id+"F4.wireOp",EDGE,"E2.bottom"),subQ0])]})]});}
            var Q2;
            Q2=makeQuery(id+"F22.opExtrude","CAP_EDGE",EDGE,{"disambiguationData":[OSD([sQuery(id+"F0.wireOp",EDGE,"E0.bottom"),sQuery(id+"F0.wireOp",EDGE,"E0.left"),sQuery(id+"F4.wireOp",EDGE,"E2.bottom"),sQuery(id+"F4.wireOp",EDGE,"E2.left"),sQuery(id+"F4.wireOp",EDGE,"E2.right")])],"isStart":false});
            var Q3;
            {var subQ0=sQuery(id+"F4.wireOp",EDGE,"E1.right");var subQ1=sQuery(id+"F4.wireOp",EDGE,"E1.bottom");var subQ2=sQuery(id+"F0.wireOp",EDGE,"E0.left");var subQ3=sQuery(id+"F0.wireOp",EDGE,"E0.bottom");Q3=makeQuery(id+"F22.opExtrude","CAP_EDGE",EDGE,{"disambiguationData":[OSD([subQ3,subQ2,subQ1,subQ0]),TDD([makeQuery(id+"F19.boolean.opBoolean","COPY",EDGE,{"derivedFrom":makeQuery(id+"F19.opExtrude","CAP_EDGE",EDGE,{"disambiguationData":[OSD([subQ3,subQ2,subQ1,subQ0])],"isStart":false})})])],"isStart":false});}
            var Q4;
            {var subQ0=sQuery(id+"F4.wireOp",EDGE,"E1.left");var subQ1=sQuery(id+"F0.wireOp",EDGE,"E0.left");var subQ2=sQuery(id+"F0.wireOp",EDGE,"E0.bottom");Q4=makeQuery(id+"F22.boolean.opBoolean","MERGE",EDGE,{"derivedFrom":[makeQuery(id+"F19.boolean.opBoolean","MERGE",EDGE,{"derivedFrom":[makeQuery(id+"F3.boolean.opBoolean","MERGE",EDGE,{"derivedFrom":[makeQuery(id+"F1.opExtrude","CAP_EDGE",EDGE,{"disambiguationData":[OSD([subQ1])],"isStart":false}),makeQuery(id+"F3.opExtrude","SWEPT_EDGE",EDGE,{"disambiguationData":[OSD([subQ2,subQ1]),TDD([makeQuery(id+"F1.opExtrude","CAP_VERTEX",VERTEX,{"disambiguationData":[OSD([subQ2,subQ1])],"isStart":false})])]})]}),makeQuery(id+"F19.opExtrude","CAP_EDGE",EDGE,{"disambiguationData":[OSD([subQ2,subQ1,sQuery(id+"F6.wireOp",EDGE,"E4.top"),sQuery(id+"F6.wireOp",EDGE,"E4.left")])],"isStart":false}),makeQuery(id+"F19.opExtrude","CAP_EDGE",EDGE,{"disambiguationData":[OSD([subQ2,subQ1,sQuery(id+"F4.wireOp",EDGE,"E1.top"),subQ0])],"isStart":false})]}),makeQuery(id+"F22.opExtrude","SWEPT_EDGE",EDGE,{"disambiguationData":[OSD([sQuery(id+"F4.wireOp",EDGE,"E1.bottom"),subQ0])]})]});}
            var Q5;
            Q5=makeQuery(id+"F19.boolean.opBoolean","COPY",EDGE,{"derivedFrom":makeQuery(id+"F19.opExtrude","CAP_EDGE",EDGE,{"disambiguationData":[OSD([sQuery(id+"F0.wireOp",EDGE,"E0.bottom"),sQuery(id+"F0.wireOp",EDGE,"E0.left"),sQuery(id+"F6.wireOp",EDGE,"E4.bottom"),sQuery(id+"F6.wireOp",EDGE,"E4.right")])],"isStart":false})});
            var Q6;
            {var subQ0=sQuery(id+"F0.wireOp",EDGE,"E0.left");var subQ1=sQuery(id+"F0.wireOp",EDGE,"E0.bottom");Q6=makeQuery(id+"F22.boolean.opBoolean","MERGE",FACE,{"derivedFrom":[makeQuery(id+"F20.boolean.opBoolean","MERGE",FACE,{"derivedFrom":[makeQuery(id+"F3.boolean.opBoolean","MERGE",FACE,{"derivedFrom":[makeQuery(id+"F2.boolean.opBoolean","MERGE",FACE,{"derivedFrom":[makeQuery(id+"F1.opExtrude","CAP_FACE",FACE,{"disambiguationData":[OSD([subQ1,sQuery(id+"F0.wireOp",EDGE,"E0.top"),subQ0,sQuery(id+"F0.wireOp",EDGE,"E0.right")])],"isStart":true}),makeQuery(id+"F2.opExtrude","SWEPT_FACE",FACE,{"disambiguationData":[OSD([subQ0]),TDD([makeQuery(id+"F1.opExtrude","CAP_EDGE",EDGE,{"disambiguationData":[OSD([subQ0])],"isStart":true})])]})]}),makeQuery(id+"F3.opExtrude","SWEPT_FACE",FACE,{"disambiguationData":[OSD([subQ1,subQ0]),TDD([makeQuery(id+"F2.boolean.opBoolean","MERGE",EDGE,{"derivedFrom":[makeQuery(id+"F1.opExtrude","CAP_EDGE",EDGE,{"disambiguationData":[OSD([subQ1])],"isStart":true}),makeQuery(id+"F2.opExtrude","SWEPT_EDGE",EDGE,{"disambiguationData":[OSD([subQ1,subQ0]),TDD([makeQuery(id+"F1.opExtrude","CAP_VERTEX",VERTEX,{"disambiguationData":[OSD([subQ1,subQ0])],"isStart":true})])]})]})])]})]}),makeQuery(id+"F20.opExtrude","SWEPT_FACE",FACE,{"disambiguationData":[OSD([subQ1,subQ0])]})]}),makeQuery(id+"F22.opExtrude","SWEPT_FACE",FACE,{"disambiguationData":[OSD([subQ1,subQ0])]})]});}
            chamfer(context, id + "F24", {"entities" : qUnion([Q0, Q1, Q2, Q3, Q4, Q5, Q6]), "width" : 1 * mm, "tangentPropagation" : true});
        }
    });
